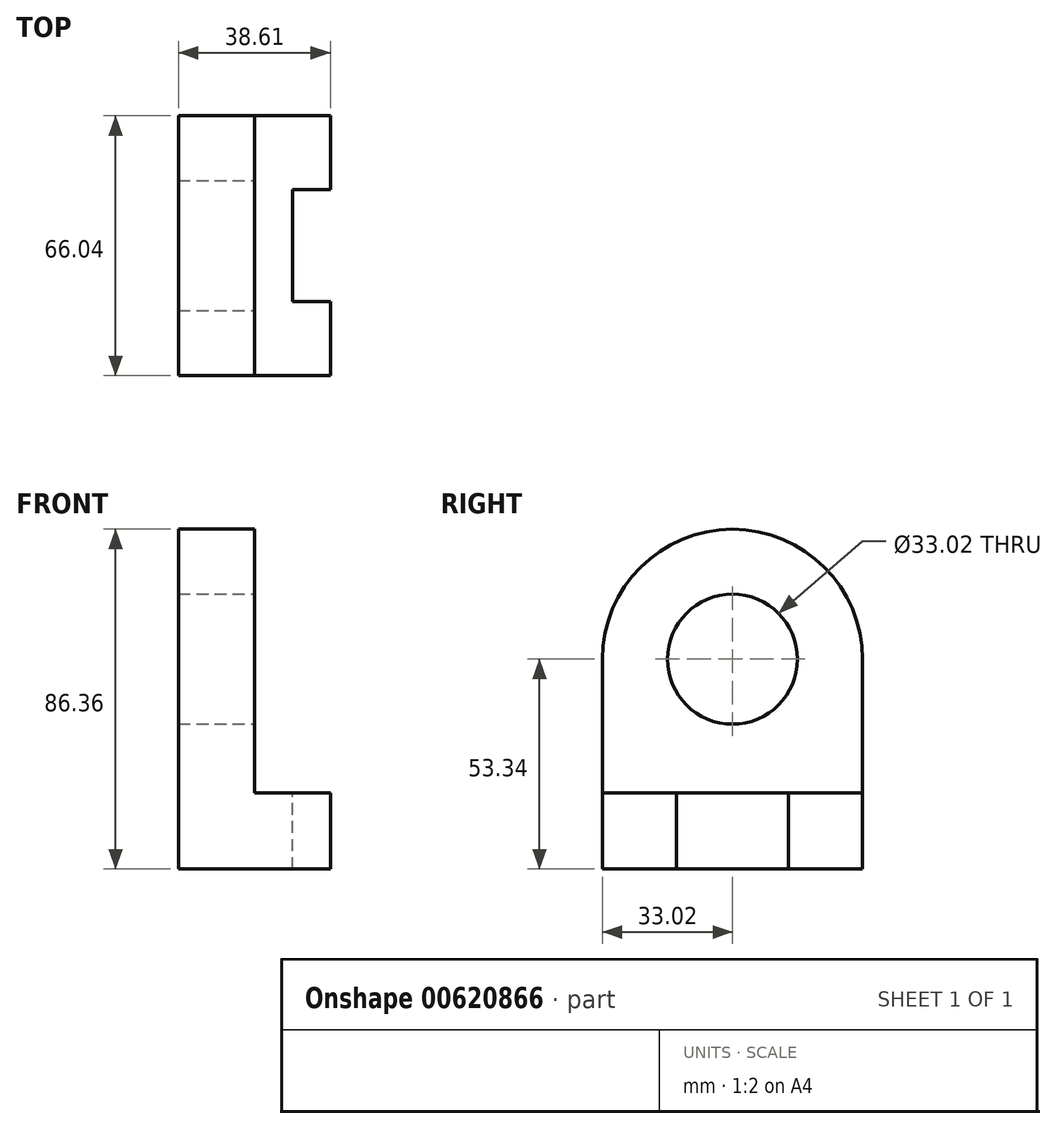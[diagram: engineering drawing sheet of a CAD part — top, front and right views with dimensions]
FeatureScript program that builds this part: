
annotation { "Feature Type Name" : "Feature", "Feature Type Description" : "" }
export const myFeature = defineFeature(function(context is Context, id is Id, definition is map)
    precondition{}
    {
        {
            var Q0;
            Q0=qCreatedBy(makeId("Front.planeOp"),FACE);
            var sketch = newSketch(context, id + "F0", { "sketchPlane" : qUnion([Q0])});
            skLineSegment(sketch, "E0", {"start": v(0, 0) * mm, "end": v(38.6, 0) * mm});
            skLineSegment(sketch, "E1", {"start": v(38.6, 0) * mm, "end": v(38.6, 19.3) * mm});
            skLineSegment(sketch, "E2", {"start": v(38.6, 19.3) * mm, "end": v(19.3, 19.3) * mm});
            skLineSegment(sketch, "E3", {"start": v(19.3, 19.3) * mm, "end": v(19.3, 86.36) * mm});
            skLineSegment(sketch, "E4", {"start": v(19.3, 86.36) * mm, "end": v(0, 86.36) * mm});
            skLineSegment(sketch, "E5", {"start": v(0, 86.36) * mm, "end": v(0, 0) * mm});
            skSolve(sketch);
        }
        {
            var Q0;
            Q0=makeQuery(id+"F0.imprint","IMPRINT",FACE,{"disambiguationData":[TD([[makeQuery(id+"F0.imprint","IMPRINT",EDGE,{"derivedFrom":sQuery(id+"F0.wireOp",EDGE,"E0")}),1.0]])]});
            extrude(context, id + "F1", {"entities" : qUnion([Q0]), "depth" : 66.04 * mm, "offsetDistance" : 25.4 * mm});
        }
        {
            var Q0;
            Q0=makeQuery(id+"F1.opExtrude","CAP_EDGE",EDGE,{"disambiguationData":[OSD([sQuery(id+"F0.wireOp",EDGE,"E4")])],"isStart":true});
            fillet(context, id + "F2", {"entities" : qUnion([Q0]), "radius" : 33.02 * mm, "tangentPropagation" : true, "allowEdgeOverflow" : false});
        }
        {
            var Q0;
            Q0=makeQuery(id+"F1.opExtrude","CAP_EDGE",EDGE,{"disambiguationData":[OSD([sQuery(id+"F0.wireOp",EDGE,"E4")])],"isStart":false});
            fillet(context, id + "F3", {"entities" : qUnion([Q0]), "radius" : 33.02 * mm, "tangentPropagation" : true, "allowEdgeOverflow" : false});
        }
        {
            var Q0;
            Q0=makeQuery(id+"F1.opExtrude","SWEPT_FACE",FACE,{"disambiguationData":[OSD([sQuery(id+"F0.wireOp",EDGE,"E3")])]});
            var sketch = newSketch(context, id + "F4", { "sketchPlane" : qUnion([Q0])});
            skCircle(sketch, "E6", {"center": v(-33.02, 53.34) * mm, "radius": 16.51 * mm});
            skSolve(sketch);
        }
        {
            var Q0;
            Q0=makeQuery(id+"F4.imprint","IMPRINT",FACE,{"disambiguationData":[TD([[makeQuery(id+"F4.imprint","IMPRINT",EDGE,{"derivedFrom":sQuery(id+"F4.wireOp",EDGE,"E6")}),1.0]])]});
            var Q1;
            Q1=sQuery(id+"F4.wireOp",EDGE,"E6");
            extrude(context, id + "F5", {"entities" : qUnion([Q0]), "operationType" : NewBodyOperationType.REMOVE, "surfaceEntities" : qUnion([Q1]), "oppositeDirection" : true, "depth" : 34.54 * mm, "offsetDistance" : 25.4 * mm});
        }
        {
            var Q0;
            Q0=makeQuery(id+"F1.opExtrude","SWEPT_FACE",FACE,{"disambiguationData":[OSD([sQuery(id+"F0.wireOp",EDGE,"E2")])]});
            var sketch = newSketch(context, id + "F6", { "sketchPlane" : qUnion([Q0])});
            skLineSegment(sketch, "E7", {"start": v(38.6, -33.02) * mm, "end": v(38.6, -18.8) * mm});
            skLineSegment(sketch, "E8", {"start": v(38.6, -18.8) * mm, "end": v(28.96, -18.8) * mm});
            skLineSegment(sketch, "E9", {"start": v(28.96, -18.8) * mm, "end": v(28.96, -47.24) * mm});
            skLineSegment(sketch, "E10", {"start": v(28.96, -47.24) * mm, "end": v(38.6, -47.24) * mm});
            skLineSegment(sketch, "E11", {"start": v(38.6, -47.24) * mm, "end": v(38.6, -33.02) * mm});
            skSolve(sketch);
        }
        {
            var Q0;
            Q0=makeQuery(id+"F6.imprint","IMPRINT",FACE,{"disambiguationData":[TD([[makeQuery(id+"F6.imprint","IMPRINT",EDGE,{"derivedFrom":sQuery(id+"F6.wireOp",EDGE,"E7")}),1.0]])]});
            extrude(context, id + "F7", {"entities" : qUnion([Q0]), "operationType" : NewBodyOperationType.REMOVE, "oppositeDirection" : true, "depth" : 25.4 * mm, "offsetDistance" : 25.4 * mm});
        }
    });
